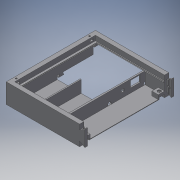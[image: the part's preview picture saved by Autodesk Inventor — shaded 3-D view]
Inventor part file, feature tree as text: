
AUTODESK INVENTOR PART (.ipt)
format: ipt  version: 2016 SP2 (Build 200236200, 236)  size: 1,032,704 bytes
history: native  units: mm
features: sketch x28, extrude x24, reference x10, projected_geometry x6, chamfer x2, thread x2, revolve x2, other x2
ambient origin geometry x8: Origin, YZ Plane, XZ Plane, XY Plane, X Axis, Y Axis, Z Axis, Center Point
bodies: Volumenkörper1 (feature_tree), Volumenkörper4 (feature_tree), Volumenkörper5 (feature_tree)
feature tree (76):
  extrude  "Extrusion1"  Depth=2.0mm TaperAngle=0.0deg
  extrude  "Extrusion2"  Depth=26.0mm TaperAngle=0.0deg
  chamfer  "Fase1"  Distance=3.0mm
  extrude  "Extrusion3"  Depth=78.5mm
  extrude  "Extrusion4"  Depth=2.5mm
  extrude  "Extrusion5"  Depth=43.5mm
  extrude  "Extrusion8"  Depth=0.5mm
  extrude  "Extrusion9"  Depth=23.0mm TaperAngle=0.0deg
  extrude  "Extrusion10"  Depth=12.0mm
  extrude  "Extrusion11"  Depth=12.0mm
  extrude  "Extrusion12"  Depth=10.0mm
  extrude  "Extrusion13"  Depth=10.0mm
  extrude  "Extrusion14"  Depth=10.0mm
  extrude  "Extrusion15"  Depth=3.5mm TaperAngle=0.0deg
  extrude  "Extrusion16"  Depth=3.0mm
  extrude  "Extrusion17"  Depth=5.8mm
  extrude  "Extrusion18"  Depth=2.5mm TaperAngle=0.0deg
  extrude  "Extrusion19"  Depth=30.0mm
  extrude  "Extrusion20"  TaperAngle=60.0deg  [1 undecoded]
  extrude  "Extrusion21"  Depth=5.0mm TaperAngle=0.0deg
  extrude  "Extrusion22"  Depth=5.0mm
  extrude  "Extrusion23"  Depth=10.0mm
  extrude  "Extrusion24"  Depth=25.0mm
  thread  "Gewinde3"  [1 undecoded]
  thread  "Gewinde4"  [1 undecoded]
  revolve  "Umdrehung3"
  other  "Spirale3"
  revolve  "Umdrehung4"
  other  "Spirale4"
  extrude  "Extrusion25"  Depth=3.0mm
  extrude  "Extrusion26"  Depth=3.0mm
  chamfer  "Fase2"  Distance=7.0mm
  sketch  "Skizze1"  dims[d0=9.3mm d1=0.0mm d2=2.0mm d3=0.0mm]
  reference  "Referenz1"
  reference  "Referenz2"
  reference  "Referenz3"
  sketch  "Skizze2"  dims[d4=1.5mm d5=2.0mm d6=45.0deg d7=26.0mm d8=0.0mm d9=3.0mm d10=0.0mm]
  reference  "Referenz4"
  sketch  "Skizze3"  dims[d15=2.0mm d16=78.5mm]
  projected_geometry  "Projizierte Kontur1"
  sketch  "Skizze4"  dims[d17=43.5mm d18=2.5mm]
  sketch  "Skizze6"  dims[d20=90.0deg d21=43.5mm]
  sketch  "Skizze9"  dims[d22=3.0mm d23=0.5mm]
  sketch  "Skizze10"  dims[d24=78.5mm d25=23.0mm d26=0.0mm]
  sketch  "Skizze11"  dims[d41=12.0mm d42=12.0mm]
  sketch  "Skizze12"  dims[d43=12.0mm d44=12.0mm]
  projected_geometry  "Projizierte Kontur2"
  projected_geometry  "Projizierte Kontur3"
  sketch  "Skizze13"  dims[d45=8.0mm d46=0.0mm d47=10.0mm]
  sketch  "Skizze14"  dims[d48=2.0mm d49=0.0mm d50=10.0mm]
  sketch  "Skizze15"  dims[d51=10.0mm d52=10.0mm]
  projected_geometry  "Projizierte Kontur4"
  sketch  "Skizze16"  dims[d53=10.0mm d54=3.5mm d55=0.0mm]
  sketch  "Skizze17"  dims[d56=3.0mm d57=3.0mm]
  sketch  "Skizze18"  dims[d62=9.25mm d63=0.0mm d64=5.8mm]
  reference  "Referenz5"
  reference  "Referenz6"
  sketch  "Skizze19"  dims[d65=5.8mm d66=2.5mm d67=0.0mm]
  sketch  "Skizze20"  dims[d68=10.0mm d69=30.0mm]
  reference  "Referenz7"
  reference  "Referenz8"
  sketch  "Skizze21"  dims[d70=60.0deg d71=60.0deg]
  sketch  "Skizze22"  dims[d72=5.0mm d73=0.0mm d74=5.0mm d75=0.0mm]
  projected_geometry  "Projizierte Kontur5"
  sketch  "Skizze27"  dims[d76=5.0mm d77=5.0mm]
  sketch  "Skizze28"  dims[d80=2.5mm d81=0.0mm d82=10.0mm]
  sketch  "Skizze29"  dims[d83=10.0mm d84=25.0mm d85=10.0mm d86=4.0mm d87=0.0mm]
  sketch  "Skizze30"  dims[d88=9.0mm d89=0.0mm d90=3.0mm]
  sketch  "Skizze31"  dims[d91=5.7mm d92=3.0mm]
  sketch  "Skizze32"  dims[d93=5.7mm]
  sketch  "Skizze33"  dims[d94=1.35mm]
  sketch  "Skizze34"  dims[d95=3.5mm d96=7.0mm d97=0.0mm]
  sketch  "Skizze35"  dims[d98=1.35mm d99=62.25mm d100=0.0mm d101=5.7mm d102=2.8mm d103=4.0mm d104=0.0mm d105=4.0mm d106=0.0mm d118=60.0deg d136=60.0deg d150=43.5mm d151=10.0mm d152=15.0mm d153=100.0mm d154=0.0mm d156=5.0mm d157=12.217305mm d158=12.217305mm d159=10.0mm d162=12.217305mm d163=10.0mm d164=12.217305mm d165=2.5mm d166=5.0mm d167=2.5mm d168=6.0mm d169=0.0mm d170=7.0mm d171=7.0mm d172=7.5mm d173=5.0mm d174=5.0mm d175=2.5mm d176=0.0mm d177=10.0mm d178=0.0mm d179=10.0mm d180=0.0mm d181=60.0deg d182=0.240125mm d183=0.240125mm d186=1.5mm d188=60.0deg d190=0.0mm d191=1.5015mm d192=7.0mm d193=10.0mm d194=0.0mm d195=0.0mm d196=0.0mm d197=0.0mm d198=0.0mm d199=60.0deg d200=0.240125mm d201=0.240125mm d204=1.5mm d206=60.0deg d208=0.0mm d209=1.5015mm d210=7.0mm d211=10.0mm d212=0.0mm d213=0.0mm d214=0.0mm d215=0.0mm d216=0.0mm d217=30.0mm d218=9.0mm d219=12.5mm d220=19.0mm d221=12.0mm d222=2.0mm d223=6.5mm d224=10.0mm d225=0.0mm d226=0.75mm d227=0.0mm d228=0.75mm d229=2.0mm d230=45.0deg d231=15.0mm d232=20.5mm]
  projected_geometry  "Projizierte Kontur6"
  reference  "Referenz9"
  reference  "Referenz10"
note: 3 required parameter values undecoded (feature->parameter linkage not recoverable at this tier; creation-order binding heuristic only, values carry confidence <= 0.55)
